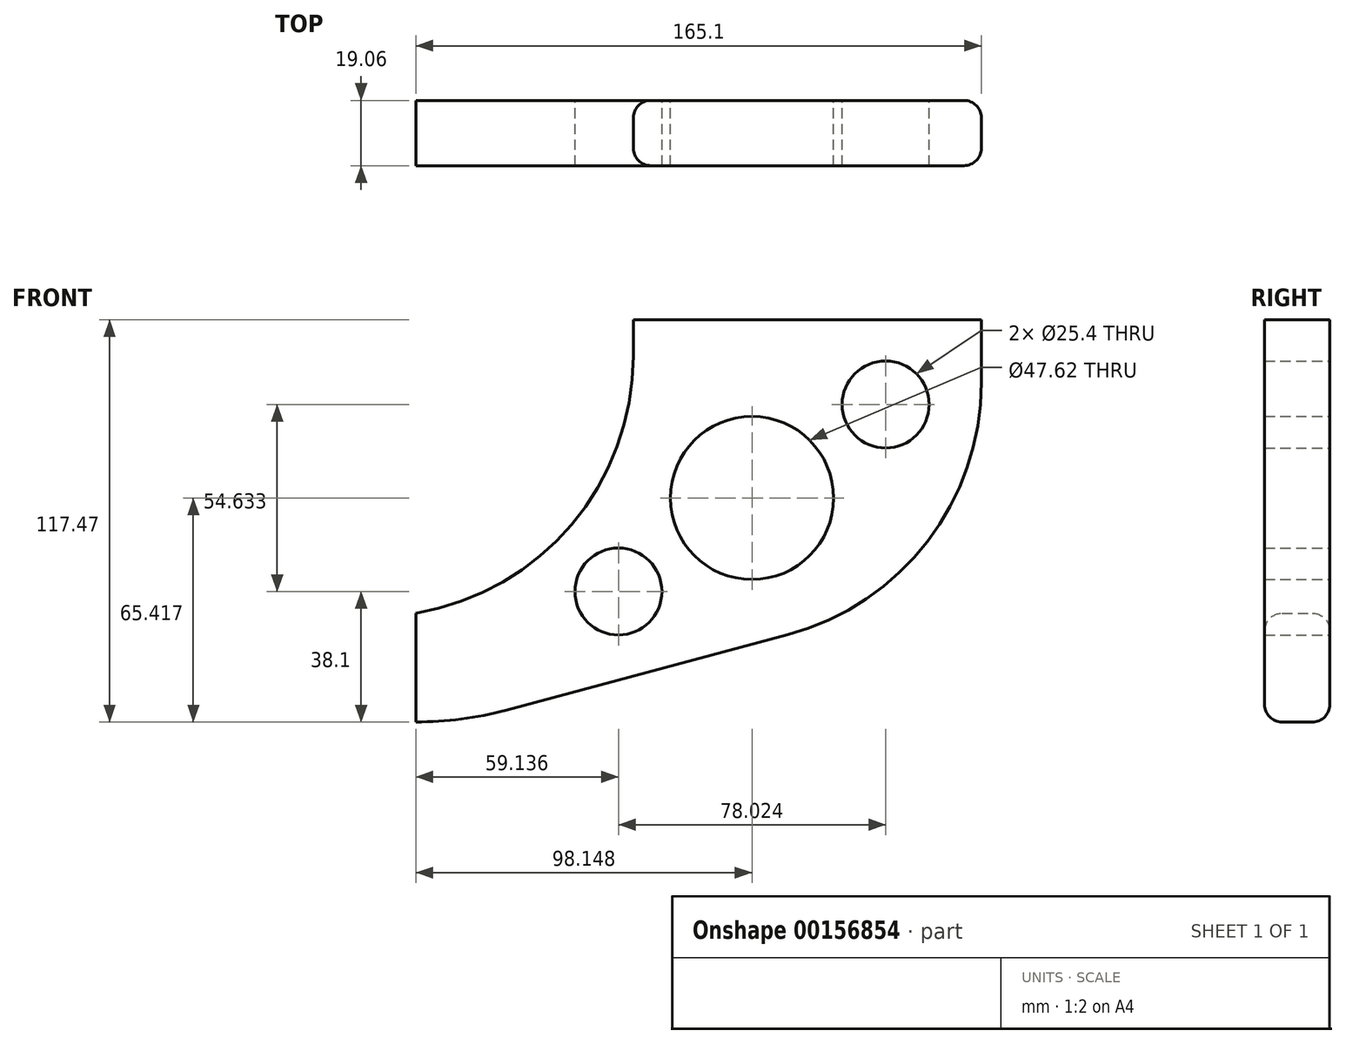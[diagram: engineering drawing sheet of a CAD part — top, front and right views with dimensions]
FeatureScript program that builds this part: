
annotation { "Feature Type Name" : "Feature", "Feature Type Description" : "" }
export const myFeature = defineFeature(function(context is Context, id is Id, definition is map)
    precondition{}
    {
        {
            var Q0;
            Q0=qCreatedBy(makeId("Front.planeOp"),FACE);
            var sketch = newSketch(context, id + "F0", { "sketchPlane" : qUnion([Q0])});
            skLineSegment(sketch, "E0", {"start": v(0, 0) * mm, "end": v(0, 31.75) * mm});
            skLineSegment(sketch, "E1", {"start": v(0, 15.88) * mm, "end": v(-20.34, 15.88) * mm});
            skPoint(sketch, "E2.oppositeSnap0", {"position": v(-10.17, 15.88) * mm});
            skLineSegment(sketch, "E2.bottom", {"start": v(-29.48, 53.97) * mm, "end": v(-10.17, 53.97) * mm, "construction": true});
            skLineSegment(sketch, "E2.top", {"start": v(-29.48, -22.22) * mm, "end": v(-10.17, -22.22) * mm, "construction": true});
            skLineSegment(sketch, "E2.left", {"start": v(-29.48, 53.97) * mm, "end": v(-29.48, -22.22) * mm, "construction": true});
            skLineSegment(sketch, "E2.right", {"start": v(-10.17, 53.97) * mm, "end": v(-10.17, -22.22) * mm, "construction": true});
            skLineSegment(sketch, "E3", {"start": v(63.5, 117.47) * mm, "end": v(165.1, 117.47) * mm});
            skLineSegment(sketch, "E4", {"start": v(108.62, 25.52) * mm, "end": v(26.3, 3.46) * mm});
            skLineSegment(sketch, "E5", {"start": v(0, 0) * mm, "end": v(0, 0) * mm});
            skPoint(sketch, "E6.visualSharp", {"position": v(13.38, 0) * mm});
            skArc(sketch, "E6.filletArc", {"start": v(0, 0) * mm, "mid": v(13.26, 0.87) * mm, "end": v(26.3, 3.46) * mm});
            skLineSegment(sketch, "E7", {"start": v(63.5, 117.47) * mm, "end": v(63.5, 106.88) * mm});
            skLineSegment(sketch, "E8", {"start": v(165.1, 117.47) * mm, "end": v(165.1, 99.12) * mm});
            skPoint(sketch, "E9.visualSharp", {"position": v(165.1, 40.65) * mm});
            skArc(sketch, "E9.filletArc", {"start": v(108.62, 25.52) * mm, "mid": v(149.35, 52.74) * mm, "end": v(165.1, 99.12) * mm});
            skCircle(sketch, "E10", {"center": v(98.15, 65.42) * mm, "radius": 23.81 * mm});
            skCircle(sketch, "E11", {"center": v(59.14, 38.1) * mm, "radius": 12.7 * mm});
            skLineSegment(sketch, "E12", {"start": v(59.14, 38.1) * mm, "end": v(137.16, 92.73) * mm});
            skCircle(sketch, "E13", {"center": v(137.16, 92.73) * mm, "radius": 12.7 * mm});
            skArc(sketch, "E14", {"start": v(0, 31.75) * mm, "mid": v(45.5, 57.7) * mm, "end": v(63.5, 106.88) * mm});
            skSolve(sketch);
        }
        {
            var Q0;
            Q0=makeQuery(id+"F0.imprint","IMPRINT",FACE,{"disambiguationData":[TD([[makeQuery(id+"F0.imprint","IMPRINT",EDGE,{"derivedFrom":sQuery(id+"F0.wireOp",EDGE,"j4vhDPAk-CAK1-qlL1-k8nX-TCheDll0MH1j")}),1.0]])]});
            var Q1;
            Q1=makeQuery(id+"F0.imprint","IMPRINT",FACE,{"disambiguationData":[TD([[makeQuery(id+"F0.imprint","IMPRINT",EDGE,{"derivedFrom":sQuery(id+"F0.wireOp",EDGE,"NmXSyMjL-h96Q-JC3t-Mk7E-inkNAQ3TzAdn")}),1.0]])]});
            var Q2;
            Q2=makeQuery(id+"F0.imprint","IMPRINT",FACE,{"disambiguationData":[TD([[makeQuery(id+"F0.imprint","IMPRINT",EDGE,{"derivedFrom":sQuery(id+"F0.wireOp",EDGE,"E3")}),-1.0]])]});
            extrude(context, id + "F1", {"entities" : qUnion([Q0, Q1, Q2]), "endBound" : BoundingType.SYMMETRIC, "depth" : 19.05 * mm});
        }
        {
            var Q0;
            Q0=makeQuery(id+"F1.opExtrude","CAP_EDGE",EDGE,{"disambiguationData":[OSD([sQuery(id+"F0.wireOp",EDGE,"E14")])],"isStart":false});
            var Q1;
            Q1=makeQuery(id+"F1.opExtrude","CAP_EDGE",EDGE,{"disambiguationData":[OSD([sQuery(id+"F0.wireOp",EDGE,"E7")])],"isStart":false});
            var Q2;
            Q2=makeQuery(id+"F1.opExtrude","CAP_EDGE",EDGE,{"disambiguationData":[OSD([sQuery(id+"F0.wireOp",EDGE,"E7")])],"isStart":true});
            var Q3;
            Q3=makeQuery(id+"F1.opExtrude","CAP_EDGE",EDGE,{"disambiguationData":[OSD([sQuery(id+"F0.wireOp",EDGE,"E8")])],"isStart":false});
            var Q4;
            Q4=makeQuery(id+"F1.opExtrude","CAP_EDGE",EDGE,{"disambiguationData":[OSD([sQuery(id+"F0.wireOp",EDGE,"E9.filletArc")])],"isStart":false});
            var Q5;
            Q5=makeQuery(id+"F1.opExtrude","CAP_EDGE",EDGE,{"disambiguationData":[OSD([sQuery(id+"F0.wireOp",EDGE,"E6.filletArc")])],"isStart":true});
            fillet(context, id + "F2", {"entities" : qUnion([Q0, Q1, Q2, Q3, Q4, Q5]), "radius" : 5.08 * mm, "tangentPropagation" : true, "allowEdgeOverflow" : false});
        }
    });
